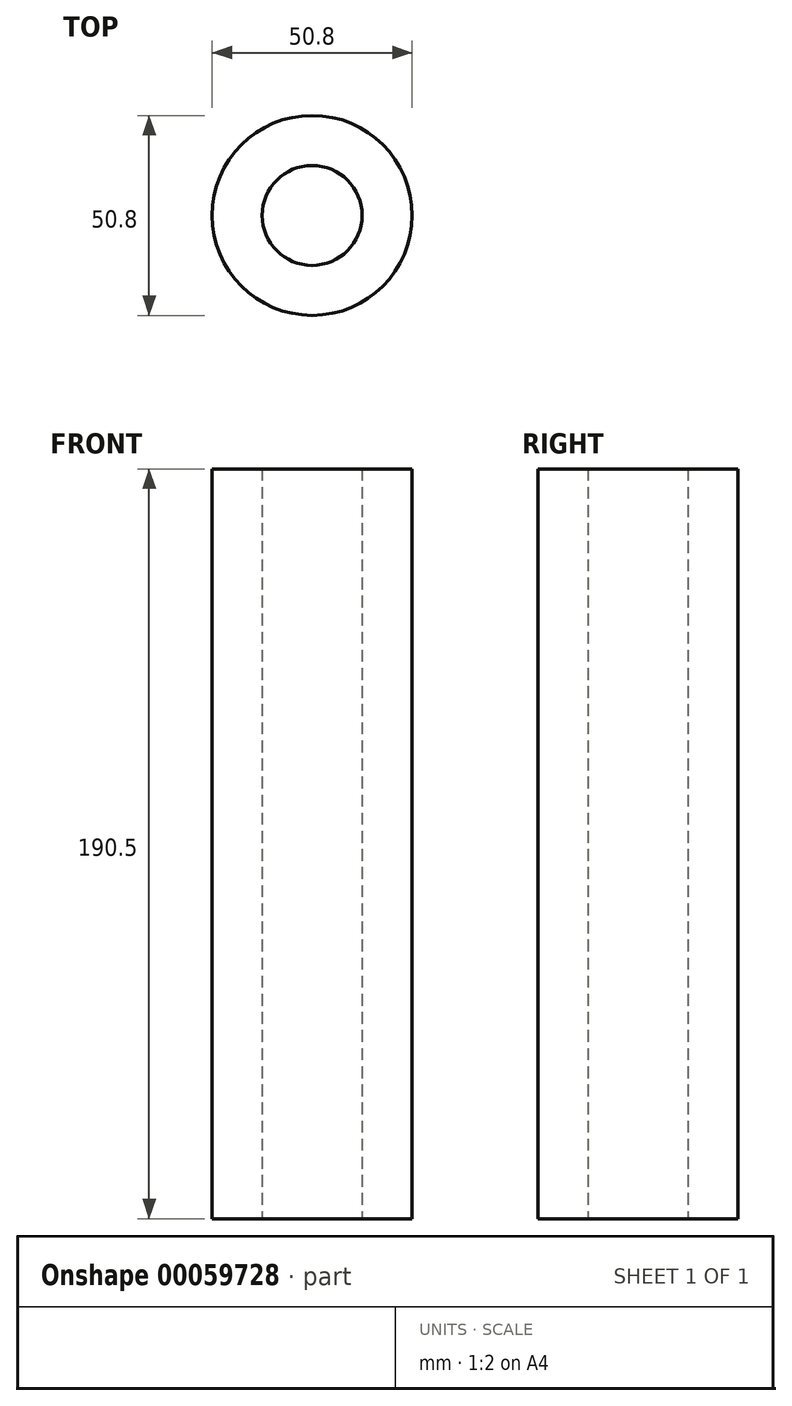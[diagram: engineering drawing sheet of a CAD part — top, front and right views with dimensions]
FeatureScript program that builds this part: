
annotation { "Feature Type Name" : "Feature", "Feature Type Description" : "" }
export const myFeature = defineFeature(function(context is Context, id is Id, definition is map)
    precondition{}
    {
        {
            var Q0;
            Q0=qCreatedBy(makeId("Top.planeOp"),FACE);
            var sketch = newSketch(context, id + "F0", { "sketchPlane" : qUnion([Q0])});
            skLineSegment(sketch, "E0", {"start": v(0, 41.64) * mm, "end": v(0, -65.02) * mm, "construction": true});
            skLineSegment(sketch, "E1", {"start": v(47.17, 0) * mm, "end": v(-61.53, 0) * mm, "construction": true});
            skCircle(sketch, "E2", {"center": v(0, 0) * mm, "radius": 25.4 * mm});
            skCircle(sketch, "E3", {"center": v(0, 0) * mm, "radius": 12.7 * mm});
            skSolve(sketch);
        }
        {
            var Q0;
            Q0=makeQuery(id+"F0.imprint","IMPRINT",FACE,{"disambiguationData":[TD([[makeQuery(id+"F0.imprint","IMPRINT",EDGE,{"derivedFrom":sQuery(id+"F0.wireOp",EDGE,"E2")}),1.0]])]});
            extrude(context, id + "F1", {"entities" : qUnion([Q0]), "endBound" : BoundingType.SYMMETRIC, "depth" : 190.5 * mm});
        }
    });
